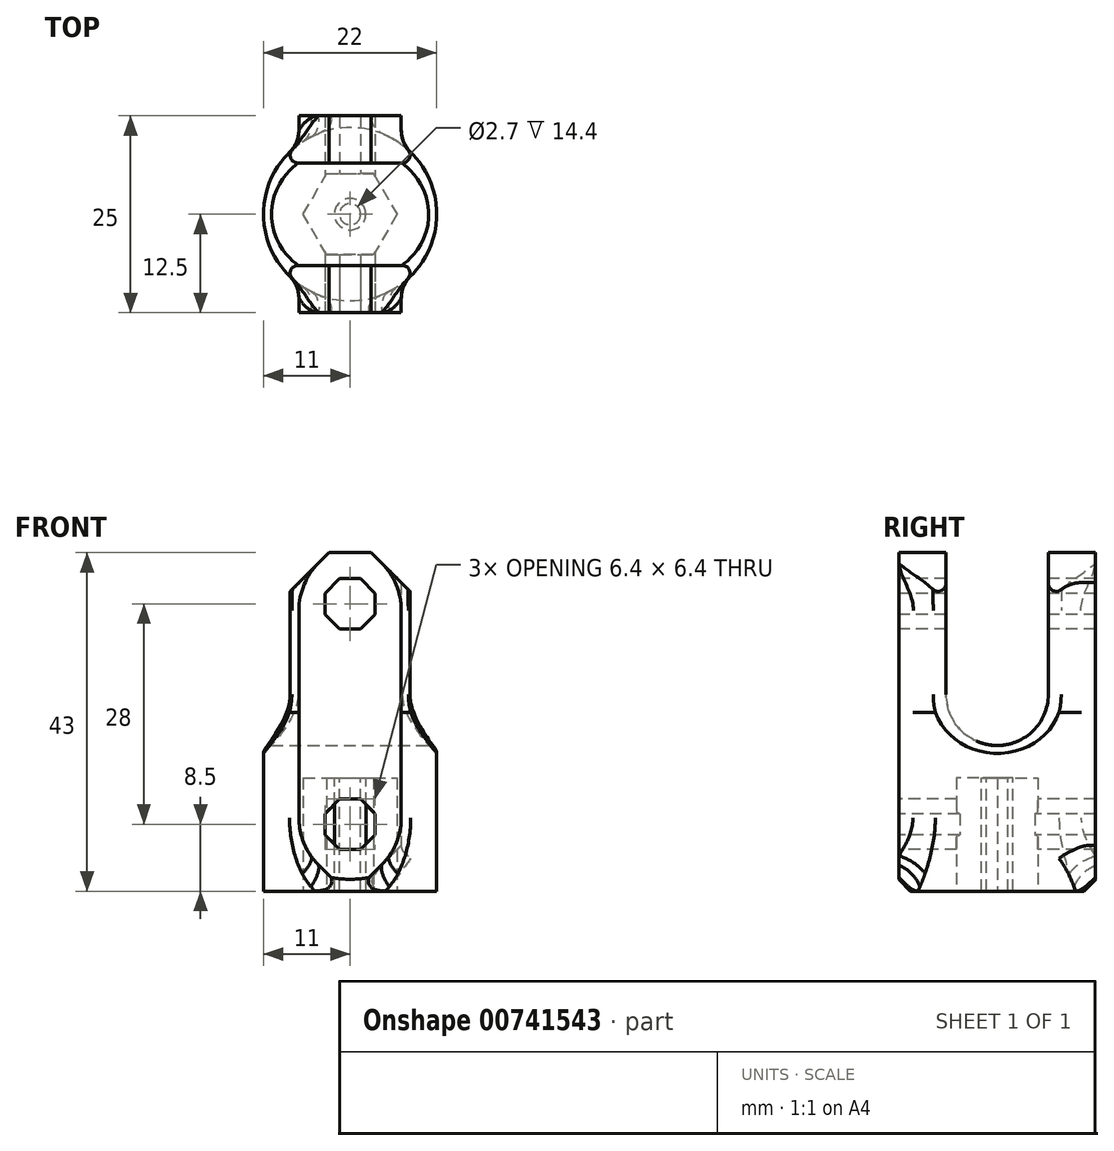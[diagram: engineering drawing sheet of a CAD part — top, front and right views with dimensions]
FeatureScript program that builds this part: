
annotation { "Feature Type Name" : "Feature", "Feature Type Description" : "" }
export const myFeature = defineFeature(function(context is Context, id is Id, definition is map)
    precondition{}
    {
        {
            var Q0;
            Q0=qCreatedBy(makeId("Top.planeOp"),FACE);
            var sketch = newSketch(context, id + "F0", { "sketchPlane" : qUnion([Q0])});
            skCircle(sketch, "E0", {"center": v(0, 0) * mm, "radius": 11 * mm});
            skCircle(sketch, "E1.cCircle", {"center": v(0, 0) * mm, "radius": 5.15 * mm, "construction": true});
            skLineSegment(sketch, "E1.0", {"start": v(-2.97, 5.15) * mm, "end": v(2.97, 5.15) * mm});
            skLineSegment(sketch, "E1.1", {"start": v(2.97, 5.15) * mm, "end": v(5.95, 0) * mm});
            skLineSegment(sketch, "E1.2", {"start": v(5.95, 0) * mm, "end": v(2.97, -5.15) * mm});
            skLineSegment(sketch, "E1.3", {"start": v(2.97, -5.15) * mm, "end": v(-2.97, -5.15) * mm});
            skLineSegment(sketch, "E1.4", {"start": v(-2.97, -5.15) * mm, "end": v(-5.95, 0) * mm});
            skLineSegment(sketch, "E1.5", {"start": v(-5.95, 0) * mm, "end": v(-2.97, 5.15) * mm});
            skPoint(sketch, "E1.0.midPoint", {"position": v(0, 5.15) * mm});
            skSolve(sketch);
        }
        {
            var Q0;
            Q0 = qSketchRegion(id + "F0", true);
            extrude(context, id + "F1", {"entities" : qUnion([Q0]), "depth" : 14 * mm, "offsetDistance" : 25 * mm});
        }
        {
            var Q0;
            Q0=makeQuery(id+"F1.opExtrude","CAP_FACE",FACE,{"disambiguationData":[OSD([sQuery(id+"F0.wireOp",EDGE,"E0"),sQuery(id+"F0.wireOp",EDGE,"E1.0"),sQuery(id+"F0.wireOp",EDGE,"E1.1"),sQuery(id+"F0.wireOp",EDGE,"E1.2"),sQuery(id+"F0.wireOp",EDGE,"E1.3"),sQuery(id+"F0.wireOp",EDGE,"E1.4"),sQuery(id+"F0.wireOp",EDGE,"E1.5")])],"isStart":false});
            var sketch = newSketch(context, id + "F2", { "sketchPlane" : qUnion([Q0])});
            skCircle(sketch, "E2.0", {"center": v(0, 0) * mm, "radius": 11 * mm});
            skSolve(sketch);
        }
        {
            var Q0;
            Q0 = qSketchRegion(id + "F2", true);
            extrude(context, id + "F3", {"entities" : qUnion([Q0]), "operationType" : NewBodyOperationType.ADD, "depth" : 29 * mm, "offsetDistance" : 25 * mm});
        }
        {
            var Q0;
            Q0=qCreatedBy(makeId("Front.planeOp"),FACE);
            var sketch = newSketch(context, id + "F4", { "sketchPlane" : qUnion([Q0])});
            skCircle(sketch, "E3.cCircle", {"center": v(0, 8.5) * mm, "radius": 6.5 * mm, "construction": true});
            skLineSegment(sketch, "E3.0", {"start": v(-2.7, 15) * mm, "end": v(2.7, 15) * mm, "construction": true});
            skLineSegment(sketch, "E3.1", {"start": v(2.7, 15) * mm, "end": v(6.5, 11.2) * mm, "construction": true});
            skLineSegment(sketch, "E3.2", {"start": v(6.5, 11.2) * mm, "end": v(6.5, 5.8) * mm});
            skLineSegment(sketch, "E3.3", {"start": v(6.5, 5.8) * mm, "end": v(2.7, 2) * mm});
            skLineSegment(sketch, "E3.4", {"start": v(2.7, 2) * mm, "end": v(-2.7, 2) * mm});
            skLineSegment(sketch, "E3.5", {"start": v(-2.7, 2) * mm, "end": v(-6.5, 5.8) * mm});
            skLineSegment(sketch, "E3.6", {"start": v(-6.5, 5.8) * mm, "end": v(-6.5, 11.2) * mm});
            skLineSegment(sketch, "E3.7", {"start": v(-6.5, 11.2) * mm, "end": v(-2.7, 15) * mm, "construction": true});
            skPoint(sketch, "E3.0.midPoint", {"position": v(0, 15) * mm});
            skPoint(sketch, "E4.0.1.0", {"position": v(0, 43) * mm});
            skLineSegment(sketch, "E4.0.1.1", {"start": v(6.5, 39.2) * mm, "end": v(6.5, 33.8) * mm});
            skLineSegment(sketch, "E4.0.1.2", {"start": v(-6.5, 33.8) * mm, "end": v(-6.5, 39.2) * mm});
            skLineSegment(sketch, "E4.0.1.3", {"start": v(-6.5, 39.2) * mm, "end": v(-2.7, 43) * mm});
            skLineSegment(sketch, "E4.0.1.4", {"start": v(2.7, 30) * mm, "end": v(-2.7, 30) * mm, "construction": true});
            skLineSegment(sketch, "E4.0.1.5", {"start": v(6.5, 33.8) * mm, "end": v(2.7, 30) * mm, "construction": true});
            skLineSegment(sketch, "E4.0.1.6", {"start": v(-2.7, 43) * mm, "end": v(2.7, 43) * mm});
            skLineSegment(sketch, "E4.0.1.7", {"start": v(2.7, 43) * mm, "end": v(6.5, 39.2) * mm});
            skLineSegment(sketch, "E4.0.1.8", {"start": v(-2.7, 30) * mm, "end": v(-6.5, 33.8) * mm, "construction": true});
            skLineSegment(sketch, "E4.direction1", {"start": v(-2.7, 2) * mm, "end": v(23.3, 2) * mm, "construction": true});
            skLineSegment(sketch, "E4.direction2", {"start": v(-2.7, 2) * mm, "end": v(-2.7, 30) * mm, "construction": true});
            skLineSegment(sketch, "E5", {"start": v(-6.5, 33.8) * mm, "end": v(-6.5, 11.2) * mm});
            skLineSegment(sketch, "E6", {"start": v(6.5, 33.8) * mm, "end": v(6.5, 11.2) * mm});
            skSolve(sketch);
        }
        {
            var Q0;
            Q0 = qSketchRegion(id + "F4", true);
            extrude(context, id + "F5", {"entities" : qUnion([Q0]), "operationType" : NewBodyOperationType.ADD, "endBound" : BoundingType.SYMMETRIC, "depth" : 25 * mm, "offsetDistance" : 25 * mm});
        }
        {
            var Q0;
            Q0=qCreatedBy(makeId("Right.planeOp"),FACE);
            var sketch = newSketch(context, id + "F6", { "sketchPlane" : qUnion([Q0])});
            skLineSegment(sketch, "E7", {"start": v(0, 43) * mm, "end": v(0, 25) * mm});
            skArc(sketch, "E8.0.startCap", {"start": v(-6.5, 43) * mm, "mid": v(0, 49.5) * mm, "end": v(6.5, 43) * mm});
            skArc(sketch, "E8.0.endCap", {"start": v(6.5, 25) * mm, "mid": v(0, 18.5) * mm, "end": v(-6.5, 25) * mm});
            skLineSegment(sketch, "E8.0.left", {"start": v(6.5, 43) * mm, "end": v(6.5, 25) * mm});
            skLineSegment(sketch, "E8.0.right", {"start": v(-6.5, 43) * mm, "end": v(-6.5, 25) * mm});
            skLineSegment(sketch, "E9", {"start": v(0, 18.5) * mm, "end": v(18, 18.5) * mm, "construction": true});
            skSolve(sketch);
        }
        {
            var Q0;
            Q0 = qSketchRegion(id + "F6", true);
            extrude(context, id + "F7", {"entities" : qUnion([Q0]), "operationType" : NewBodyOperationType.REMOVE, "endBound" : BoundingType.SYMMETRIC, "oppositeDirection" : true, "depth" : 25 * mm, "offsetDistance" : 25 * mm});
        }
        {
            var Q0;
            Q0=qCreatedBy(makeId("Front.planeOp"),FACE);
            var sketch = newSketch(context, id + "F8", { "sketchPlane" : qUnion([Q0])});
            skCircle(sketch, "E10.cCircle", {"center": v(0, 8.5) * mm, "radius": 3.2 * mm, "construction": true});
            skLineSegment(sketch, "E10.0", {"start": v(-1.33, 11.7) * mm, "end": v(1.33, 11.7) * mm});
            skLineSegment(sketch, "E10.1", {"start": v(1.33, 11.7) * mm, "end": v(3.2, 9.83) * mm});
            skLineSegment(sketch, "E10.2", {"start": v(3.2, 9.83) * mm, "end": v(3.2, 7.17) * mm});
            skLineSegment(sketch, "E10.3", {"start": v(3.2, 7.17) * mm, "end": v(1.33, 5.3) * mm});
            skLineSegment(sketch, "E10.4", {"start": v(1.33, 5.3) * mm, "end": v(-1.33, 5.3) * mm});
            skLineSegment(sketch, "E10.5", {"start": v(-1.33, 5.3) * mm, "end": v(-3.2, 7.17) * mm});
            skLineSegment(sketch, "E10.6", {"start": v(-3.2, 7.17) * mm, "end": v(-3.2, 9.83) * mm});
            skLineSegment(sketch, "E10.7", {"start": v(-3.2, 9.83) * mm, "end": v(-1.33, 11.7) * mm});
            skPoint(sketch, "E10.0.midPoint", {"position": v(0, 11.7) * mm});
            skLineSegment(sketch, "E11.0.1.0", {"start": v(-3.2, 37.83) * mm, "end": v(-1.33, 39.7) * mm});
            skLineSegment(sketch, "E11.0.1.1", {"start": v(-3.2, 35.17) * mm, "end": v(-3.2, 37.83) * mm});
            skLineSegment(sketch, "E11.0.1.2", {"start": v(-1.33, 39.7) * mm, "end": v(1.33, 39.7) * mm});
            skLineSegment(sketch, "E11.0.1.3", {"start": v(1.33, 39.7) * mm, "end": v(3.2, 37.83) * mm});
            skLineSegment(sketch, "E11.0.1.4", {"start": v(3.2, 37.83) * mm, "end": v(3.2, 35.17) * mm});
            skLineSegment(sketch, "E11.0.1.5", {"start": v(3.2, 35.17) * mm, "end": v(1.33, 33.3) * mm});
            skLineSegment(sketch, "E11.0.1.6", {"start": v(1.33, 33.3) * mm, "end": v(-1.33, 33.3) * mm});
            skLineSegment(sketch, "E11.0.1.7", {"start": v(-1.33, 33.3) * mm, "end": v(-3.2, 35.17) * mm});
            skLineSegment(sketch, "E11.direction1", {"start": v(-1.33, 5.3) * mm, "end": v(23.67, 5.3) * mm, "construction": true});
            skLineSegment(sketch, "E11.direction2", {"start": v(-1.33, 5.3) * mm, "end": v(-1.33, 33.3) * mm, "construction": true});
            skLineSegment(sketch, "E12", {"start": v(2.7, 43) * mm, "end": v(-2.7, 43) * mm});
            skLineSegment(sketch, "E13", {"start": v(-2.7, 43) * mm, "end": v(-8.87, 36.82) * mm});
            skLineSegment(sketch, "E14", {"start": v(-8.87, 36.82) * mm, "end": v(-8.87, 43.83) * mm});
            skLineSegment(sketch, "E15", {"start": v(-8.87, 43.83) * mm, "end": v(8.87, 43.83) * mm});
            skLineSegment(sketch, "E16", {"start": v(8.87, 43.83) * mm, "end": v(8.87, 36.82) * mm});
            skLineSegment(sketch, "E17", {"start": v(8.87, 36.82) * mm, "end": v(2.7, 43) * mm});
            skSolve(sketch);
        }
        {
            var Q0;
            Q0 = qSketchRegion(id + "F8", true);
            extrude(context, id + "F9", {"entities" : qUnion([Q0]), "operationType" : NewBodyOperationType.REMOVE, "endBound" : BoundingType.SYMMETRIC, "oppositeDirection" : true, "depth" : 30 * mm, "offsetDistance" : 25 * mm});
        }
        {
            var Q0;
            Q0=makeQuery(id+"F1.opExtrude","CAP_FACE",FACE,{"disambiguationData":[OSD([sQuery(id+"F0.wireOp",EDGE,"E0"),sQuery(id+"F0.wireOp",EDGE,"E1.0"),sQuery(id+"F0.wireOp",EDGE,"E1.1"),sQuery(id+"F0.wireOp",EDGE,"E1.2"),sQuery(id+"F0.wireOp",EDGE,"E1.3"),sQuery(id+"F0.wireOp",EDGE,"E1.4"),sQuery(id+"F0.wireOp",EDGE,"E1.5")])],"isStart":true});
            var sketch = newSketch(context, id + "F10", { "sketchPlane" : qUnion([Q0])});
            skCircle(sketch, "E18.cCircle", {"center": v(0, 0) * mm, "radius": 5.15 * mm, "construction": true});
            skLineSegment(sketch, "E18.0", {"start": v(2.97, 5.15) * mm, "end": v(5.95, 0) * mm});
            skLineSegment(sketch, "E18.1", {"start": v(5.95, 0) * mm, "end": v(2.97, -5.15) * mm});
            skLineSegment(sketch, "E18.2", {"start": v(2.97, -5.15) * mm, "end": v(-2.97, -5.15) * mm});
            skLineSegment(sketch, "E18.3", {"start": v(-2.97, -5.15) * mm, "end": v(-5.95, 0) * mm});
            skLineSegment(sketch, "E18.4", {"start": v(-5.95, 0) * mm, "end": v(-2.97, 5.15) * mm});
            skLineSegment(sketch, "E18.5", {"start": v(-2.97, 5.15) * mm, "end": v(2.97, 5.15) * mm});
            skPoint(sketch, "E18.0.midPoint", {"position": v(4.46, 2.57) * mm});
            skSolve(sketch);
        }
        {
            var Q0;
            Q0 = qSketchRegion(id + "F10", true);
            extrude(context, id + "F11", {"entities" : qUnion([Q0]), "operationType" : NewBodyOperationType.REMOVE, "oppositeDirection" : true, "depth" : 14.4 * mm, "offsetDistance" : 25 * mm});
        }
        {
            var Q0;
            Q0=makeQuery(id+"F7.boolean.opBoolean","INTERSECT",EDGE,{"disambiguationData":[OD(1.0)],"derivedFrom":[makeQuery(id+"F3.boolean.opBoolean","MERGE",FACE,{"derivedFrom":[makeQuery(id+"F1.opExtrude","SWEPT_FACE",FACE,{"disambiguationData":[OSD([sQuery(id+"F0.wireOp",EDGE,"E0")])]}),makeQuery(id+"F3.opExtrude","SWEPT_FACE",FACE,{"disambiguationData":[OSD([sQuery(id+"F2.wireOp",EDGE,"E2.0")])]})]}),makeQuery(id+"F7.opExtrude","SWEPT_FACE",FACE,{"disambiguationData":[OSD([sQuery(id+"F6.wireOp",EDGE,"E8.0.endCap")])]})]});
            var Q1;
            Q1=makeQuery(id+"F7.boolean.opBoolean","INTERSECT",EDGE,{"disambiguationData":[OD(1.0)],"derivedFrom":[makeQuery(id+"F3.boolean.opBoolean","MERGE",FACE,{"derivedFrom":[makeQuery(id+"F1.opExtrude","SWEPT_FACE",FACE,{"disambiguationData":[OSD([sQuery(id+"F0.wireOp",EDGE,"E0")])]}),makeQuery(id+"F3.opExtrude","SWEPT_FACE",FACE,{"disambiguationData":[OSD([sQuery(id+"F2.wireOp",EDGE,"E2.0")])]})]}),makeQuery(id+"F7.opExtrude","SWEPT_FACE",FACE,{"disambiguationData":[OSD([sQuery(id+"F6.wireOp",EDGE,"E8.0.left")])]})]});
            var Q2;
            Q2=makeQuery(id+"F7.boolean.opBoolean","INTERSECT",EDGE,{"disambiguationData":[OD(1.0)],"derivedFrom":[makeQuery(id+"F3.boolean.opBoolean","MERGE",FACE,{"derivedFrom":[makeQuery(id+"F1.opExtrude","SWEPT_FACE",FACE,{"disambiguationData":[OSD([sQuery(id+"F0.wireOp",EDGE,"E0")])]}),makeQuery(id+"F3.opExtrude","SWEPT_FACE",FACE,{"disambiguationData":[OSD([sQuery(id+"F2.wireOp",EDGE,"E2.0")])]})]}),makeQuery(id+"F7.opExtrude","SWEPT_FACE",FACE,{"disambiguationData":[OSD([sQuery(id+"F6.wireOp",EDGE,"E8.0.right")])]})]});
            var Q3;
            Q3=makeQuery(id+"F7.boolean.opBoolean","INTERSECT",EDGE,{"disambiguationData":[OD(0.0)],"derivedFrom":[makeQuery(id+"F3.boolean.opBoolean","MERGE",FACE,{"derivedFrom":[makeQuery(id+"F1.opExtrude","SWEPT_FACE",FACE,{"disambiguationData":[OSD([sQuery(id+"F0.wireOp",EDGE,"E0")])]}),makeQuery(id+"F3.opExtrude","SWEPT_FACE",FACE,{"disambiguationData":[OSD([sQuery(id+"F2.wireOp",EDGE,"E2.0")])]})]}),makeQuery(id+"F7.opExtrude","SWEPT_FACE",FACE,{"disambiguationData":[OSD([sQuery(id+"F6.wireOp",EDGE,"E8.0.endCap")])]})]});
            var Q4;
            Q4=makeQuery(id+"F7.boolean.opBoolean","INTERSECT",EDGE,{"disambiguationData":[OD(0.0)],"derivedFrom":[makeQuery(id+"F3.boolean.opBoolean","MERGE",FACE,{"derivedFrom":[makeQuery(id+"F1.opExtrude","SWEPT_FACE",FACE,{"disambiguationData":[OSD([sQuery(id+"F0.wireOp",EDGE,"E0")])]}),makeQuery(id+"F3.opExtrude","SWEPT_FACE",FACE,{"disambiguationData":[OSD([sQuery(id+"F2.wireOp",EDGE,"E2.0")])]})]}),makeQuery(id+"F7.opExtrude","SWEPT_FACE",FACE,{"disambiguationData":[OSD([sQuery(id+"F6.wireOp",EDGE,"E8.0.right")])]})]});
            var Q5;
            Q5=makeQuery(id+"F7.boolean.opBoolean","INTERSECT",EDGE,{"disambiguationData":[OD(0.0)],"derivedFrom":[makeQuery(id+"F3.boolean.opBoolean","MERGE",FACE,{"derivedFrom":[makeQuery(id+"F1.opExtrude","SWEPT_FACE",FACE,{"disambiguationData":[OSD([sQuery(id+"F0.wireOp",EDGE,"E0")])]}),makeQuery(id+"F3.opExtrude","SWEPT_FACE",FACE,{"disambiguationData":[OSD([sQuery(id+"F2.wireOp",EDGE,"E2.0")])]})]}),makeQuery(id+"F7.opExtrude","SWEPT_FACE",FACE,{"disambiguationData":[OSD([sQuery(id+"F6.wireOp",EDGE,"E8.0.left")])]})]});
            fillet(context, id + "F12", {"entities" : qUnion([Q0, Q1, Q2, Q3, Q4, Q5]), "radius" : 1 * mm, "allowEdgeOverflow" : false});
        }
        {
            var Q0;
            Q0=makeQuery(id+"F5.boolean.opBoolean","INTERSECT",EDGE,{"disambiguationData":[OD(1.0)],"derivedFrom":[makeQuery(id+"F3.boolean.opBoolean","MERGE",FACE,{"derivedFrom":[makeQuery(id+"F1.opExtrude","SWEPT_FACE",FACE,{"disambiguationData":[OSD([sQuery(id+"F0.wireOp",EDGE,"E0")])]}),makeQuery(id+"F3.opExtrude","SWEPT_FACE",FACE,{"disambiguationData":[OSD([sQuery(id+"F2.wireOp",EDGE,"E2.0")])]})]}),makeQuery(id+"F5.opExtrude","SWEPT_FACE",FACE,{"disambiguationData":[OSD([sQuery(id+"F4.wireOp",EDGE,"E3.4")])]})]});
            var Q1;
            Q1=makeQuery(id+"F5.boolean.opBoolean","INTERSECT",EDGE,{"disambiguationData":[OD(1.0)],"derivedFrom":[makeQuery(id+"F3.boolean.opBoolean","MERGE",FACE,{"derivedFrom":[makeQuery(id+"F1.opExtrude","SWEPT_FACE",FACE,{"disambiguationData":[OSD([sQuery(id+"F0.wireOp",EDGE,"E0")])]}),makeQuery(id+"F3.opExtrude","SWEPT_FACE",FACE,{"disambiguationData":[OSD([sQuery(id+"F2.wireOp",EDGE,"E2.0")])]})]}),makeQuery(id+"F5.opExtrude","SWEPT_FACE",FACE,{"disambiguationData":[OSD([sQuery(id+"F4.wireOp",EDGE,"E4.0.1.4")])]})]});
            var Q2;
            Q2=makeQuery(id+"F5.boolean.opBoolean","INTERSECT",EDGE,{"disambiguationData":[OD(0.0)],"derivedFrom":[makeQuery(id+"F3.boolean.opBoolean","MERGE",FACE,{"derivedFrom":[makeQuery(id+"F1.opExtrude","SWEPT_FACE",FACE,{"disambiguationData":[OSD([sQuery(id+"F0.wireOp",EDGE,"E0")])]}),makeQuery(id+"F3.opExtrude","SWEPT_FACE",FACE,{"disambiguationData":[OSD([sQuery(id+"F2.wireOp",EDGE,"E2.0")])]})]}),makeQuery(id+"F5.opExtrude","SWEPT_FACE",FACE,{"disambiguationData":[OSD([sQuery(id+"F4.wireOp",EDGE,"E3.4")])]})]});
            var Q3;
            Q3=makeQuery(id+"F5.boolean.opBoolean","INTERSECT",EDGE,{"disambiguationData":[OD(0.0)],"derivedFrom":[makeQuery(id+"F3.boolean.opBoolean","MERGE",FACE,{"derivedFrom":[makeQuery(id+"F1.opExtrude","SWEPT_FACE",FACE,{"disambiguationData":[OSD([sQuery(id+"F0.wireOp",EDGE,"E0")])]}),makeQuery(id+"F3.opExtrude","SWEPT_FACE",FACE,{"disambiguationData":[OSD([sQuery(id+"F2.wireOp",EDGE,"E2.0")])]})]}),makeQuery(id+"F5.opExtrude","SWEPT_FACE",FACE,{"disambiguationData":[OSD([sQuery(id+"F4.wireOp",EDGE,"E4.0.1.4")])]})]});
            var Q4;
            Q4=makeQuery(id+"F5.boolean.opBoolean","INTERSECT",EDGE,{"disambiguationData":[OD(0.0)],"derivedFrom":[makeQuery(id+"F3.boolean.opBoolean","MERGE",FACE,{"derivedFrom":[makeQuery(id+"F1.opExtrude","SWEPT_FACE",FACE,{"disambiguationData":[OSD([sQuery(id+"F0.wireOp",EDGE,"E0")])]}),makeQuery(id+"F3.opExtrude","SWEPT_FACE",FACE,{"disambiguationData":[OSD([sQuery(id+"F2.wireOp",EDGE,"E2.0")])]})]}),makeQuery(id+"F5.opExtrude","SWEPT_FACE",FACE,{"disambiguationData":[OSD([sQuery(id+"F4.wireOp",EDGE,"E3.0")])]})]});
            var Q5;
            Q5=makeQuery(id+"F5.boolean.opBoolean","INTERSECT",EDGE,{"disambiguationData":[OD(1.0)],"derivedFrom":[makeQuery(id+"F3.boolean.opBoolean","MERGE",FACE,{"derivedFrom":[makeQuery(id+"F1.opExtrude","SWEPT_FACE",FACE,{"disambiguationData":[OSD([sQuery(id+"F0.wireOp",EDGE,"E0")])]}),makeQuery(id+"F3.opExtrude","SWEPT_FACE",FACE,{"disambiguationData":[OSD([sQuery(id+"F2.wireOp",EDGE,"E2.0")])]})]}),makeQuery(id+"F5.opExtrude","SWEPT_FACE",FACE,{"disambiguationData":[OSD([sQuery(id+"F4.wireOp",EDGE,"E3.0")])]})]});
            chamfer(context, id + "F13", {"entities" : qUnion([Q0, Q1, Q2, Q3, Q4, Q5]), "width" : 2 * mm, "tangentPropagation" : true});
        }
        {
            var Q0;
            {var subQ0=sQuery(id+"F4.wireOp",EDGE,"E6");var subQ1=sQuery(id+"F4.wireOp",EDGE,"E4.0.1.1");var subQ2=sQuery(id+"F4.wireOp",EDGE,"E3.2");var subQ3=sQuery(id+"F4.wireOp",EDGE,"E4.0.1.7");Q0=makeQuery(id+"F5.boolean.opBoolean","SPLIT",EDGE,{"disambiguationData":[TD([makeQuery(id+"F5.opExtrude","CAP_FACE",FACE,{"disambiguationData":[OSD([subQ2,sQuery(id+"F4.wireOp",EDGE,"E3.3"),sQuery(id+"F4.wireOp",EDGE,"E3.4"),sQuery(id+"F4.wireOp",EDGE,"E3.5"),sQuery(id+"F4.wireOp",EDGE,"E3.6"),subQ1,sQuery(id+"F4.wireOp",EDGE,"E4.0.1.2"),sQuery(id+"F4.wireOp",EDGE,"E4.0.1.3"),sQuery(id+"F4.wireOp",EDGE,"E4.0.1.6"),subQ3,sQuery(id+"F4.wireOp",EDGE,"E5"),subQ0])],"isStart":false})])],"derivedFrom":makeQuery(id+"F5.opExtrude","SWEPT_EDGE",EDGE,{"disambiguationData":[OSD([subQ1,subQ3])]})});}
            var Q1;
            {var subQ0=sQuery(id+"F4.wireOp",EDGE,"E6");var subQ1=sQuery(id+"F4.wireOp",EDGE,"E4.0.1.1");var subQ2=sQuery(id+"F4.wireOp",EDGE,"E3.2");var subQ3=sQuery(id+"F4.wireOp",EDGE,"E3.3");Q1=makeQuery(id+"F5.boolean.opBoolean","SPLIT",EDGE,{"disambiguationData":[TD([makeQuery(id+"F5.opExtrude","CAP_FACE",FACE,{"disambiguationData":[OSD([subQ2,subQ3,sQuery(id+"F4.wireOp",EDGE,"E3.4"),sQuery(id+"F4.wireOp",EDGE,"E3.5"),sQuery(id+"F4.wireOp",EDGE,"E3.6"),subQ1,sQuery(id+"F4.wireOp",EDGE,"E4.0.1.2"),sQuery(id+"F4.wireOp",EDGE,"E4.0.1.3"),sQuery(id+"F4.wireOp",EDGE,"E4.0.1.6"),sQuery(id+"F4.wireOp",EDGE,"E4.0.1.7"),sQuery(id+"F4.wireOp",EDGE,"E5"),subQ0])],"isStart":false})])],"derivedFrom":makeQuery(id+"F5.opExtrude","SWEPT_EDGE",EDGE,{"disambiguationData":[OSD([subQ2,subQ3])]})});}
            var Q2;
            {var subQ0=sQuery(id+"F4.wireOp",EDGE,"E3.5");var subQ1=sQuery(id+"F4.wireOp",EDGE,"E5");var subQ2=sQuery(id+"F4.wireOp",EDGE,"E4.0.1.2");var subQ3=sQuery(id+"F4.wireOp",EDGE,"E3.6");Q2=makeQuery(id+"F5.boolean.opBoolean","SPLIT",EDGE,{"disambiguationData":[TD([makeQuery(id+"F5.opExtrude","CAP_FACE",FACE,{"disambiguationData":[OSD([sQuery(id+"F4.wireOp",EDGE,"E3.2"),sQuery(id+"F4.wireOp",EDGE,"E3.3"),sQuery(id+"F4.wireOp",EDGE,"E3.4"),subQ0,subQ3,sQuery(id+"F4.wireOp",EDGE,"E4.0.1.1"),subQ2,sQuery(id+"F4.wireOp",EDGE,"E4.0.1.3"),sQuery(id+"F4.wireOp",EDGE,"E4.0.1.6"),sQuery(id+"F4.wireOp",EDGE,"E4.0.1.7"),subQ1,sQuery(id+"F4.wireOp",EDGE,"E6")])],"isStart":false})])],"derivedFrom":makeQuery(id+"F5.opExtrude","SWEPT_EDGE",EDGE,{"disambiguationData":[OSD([subQ0,subQ3])]})});}
            var Q3;
            {var subQ0=sQuery(id+"F4.wireOp",EDGE,"E3.5");var subQ1=sQuery(id+"F4.wireOp",EDGE,"E5");var subQ2=sQuery(id+"F4.wireOp",EDGE,"E4.0.1.2");var subQ3=sQuery(id+"F4.wireOp",EDGE,"E3.6");Q3=makeQuery(id+"F5.boolean.opBoolean","SPLIT",EDGE,{"disambiguationData":[TD([makeQuery(id+"F5.opExtrude","CAP_FACE",FACE,{"disambiguationData":[OSD([sQuery(id+"F4.wireOp",EDGE,"E3.2"),sQuery(id+"F4.wireOp",EDGE,"E3.3"),sQuery(id+"F4.wireOp",EDGE,"E3.4"),subQ0,subQ3,sQuery(id+"F4.wireOp",EDGE,"E4.0.1.1"),subQ2,sQuery(id+"F4.wireOp",EDGE,"E4.0.1.3"),sQuery(id+"F4.wireOp",EDGE,"E4.0.1.6"),sQuery(id+"F4.wireOp",EDGE,"E4.0.1.7"),subQ1,sQuery(id+"F4.wireOp",EDGE,"E6")])],"isStart":true})])],"derivedFrom":makeQuery(id+"F5.opExtrude","SWEPT_EDGE",EDGE,{"disambiguationData":[OSD([subQ0,subQ3])]})});}
            var Q4;
            {var subQ0=sQuery(id+"F4.wireOp",EDGE,"E5");var subQ1=sQuery(id+"F4.wireOp",EDGE,"E4.0.1.2");var subQ2=sQuery(id+"F4.wireOp",EDGE,"E3.6");var subQ3=sQuery(id+"F4.wireOp",EDGE,"E4.0.1.3");Q4=makeQuery(id+"F5.boolean.opBoolean","SPLIT",EDGE,{"disambiguationData":[TD([makeQuery(id+"F5.opExtrude","CAP_FACE",FACE,{"disambiguationData":[OSD([sQuery(id+"F4.wireOp",EDGE,"E3.2"),sQuery(id+"F4.wireOp",EDGE,"E3.3"),sQuery(id+"F4.wireOp",EDGE,"E3.4"),sQuery(id+"F4.wireOp",EDGE,"E3.5"),subQ2,sQuery(id+"F4.wireOp",EDGE,"E4.0.1.1"),subQ1,subQ3,sQuery(id+"F4.wireOp",EDGE,"E4.0.1.6"),sQuery(id+"F4.wireOp",EDGE,"E4.0.1.7"),subQ0,sQuery(id+"F4.wireOp",EDGE,"E6")])],"isStart":false})])],"derivedFrom":makeQuery(id+"F5.opExtrude","SWEPT_EDGE",EDGE,{"disambiguationData":[OSD([subQ1,subQ3])]})});}
            var Q5;
            {var subQ0=sQuery(id+"F4.wireOp",EDGE,"E5");var subQ1=sQuery(id+"F4.wireOp",EDGE,"E4.0.1.3");var subQ2=sQuery(id+"F4.wireOp",EDGE,"E4.0.1.2");var subQ3=sQuery(id+"F4.wireOp",EDGE,"E3.6");Q5=makeQuery(id+"F5.boolean.opBoolean","SPLIT",EDGE,{"disambiguationData":[TD([makeQuery(id+"F5.opExtrude","CAP_FACE",FACE,{"disambiguationData":[OSD([sQuery(id+"F4.wireOp",EDGE,"E3.2"),sQuery(id+"F4.wireOp",EDGE,"E3.3"),sQuery(id+"F4.wireOp",EDGE,"E3.4"),sQuery(id+"F4.wireOp",EDGE,"E3.5"),subQ3,sQuery(id+"F4.wireOp",EDGE,"E4.0.1.1"),subQ2,subQ1,sQuery(id+"F4.wireOp",EDGE,"E4.0.1.6"),sQuery(id+"F4.wireOp",EDGE,"E4.0.1.7"),subQ0,sQuery(id+"F4.wireOp",EDGE,"E6")])],"isStart":true})])],"derivedFrom":makeQuery(id+"F5.opExtrude","SWEPT_EDGE",EDGE,{"disambiguationData":[OSD([subQ2,subQ1])]})});}
            fillet(context, id + "F14", {"entities" : qUnion([Q0, Q1, Q2, Q3, Q4, Q5]), "radius" : 8.5 * mm, "tangentPropagation" : true, "allowEdgeOverflow" : false});
        }
        {
            var Q0;
            Q0=makeQuery(id+"F5.boolean.opBoolean","INTERSECT",EDGE,{"disambiguationData":[OD(1.0)],"derivedFrom":[makeQuery(id+"F3.boolean.opBoolean","MERGE",FACE,{"derivedFrom":[makeQuery(id+"F1.opExtrude","SWEPT_FACE",FACE,{"disambiguationData":[OSD([sQuery(id+"F0.wireOp",EDGE,"E0")])]}),makeQuery(id+"F3.opExtrude","SWEPT_FACE",FACE,{"disambiguationData":[OSD([sQuery(id+"F2.wireOp",EDGE,"E2.0")])]})]}),makeQuery(id+"F5.opExtrude","SWEPT_FACE",FACE,{"disambiguationData":[OSD([sQuery(id+"F4.wireOp",EDGE,"E4.0.1.2")])]})]});
            var Q1;
            Q1=makeQuery(id+"F5.boolean.opBoolean","INTERSECT",EDGE,{"disambiguationData":[OD(1.0)],"derivedFrom":[makeQuery(id+"F3.boolean.opBoolean","MERGE",FACE,{"derivedFrom":[makeQuery(id+"F1.opExtrude","SWEPT_FACE",FACE,{"disambiguationData":[OSD([sQuery(id+"F0.wireOp",EDGE,"E0")])]}),makeQuery(id+"F3.opExtrude","SWEPT_FACE",FACE,{"disambiguationData":[OSD([sQuery(id+"F2.wireOp",EDGE,"E2.0")])]})]}),makeQuery(id+"F5.opExtrude","SWEPT_FACE",FACE,{"disambiguationData":[OSD([sQuery(id+"F4.wireOp",EDGE,"E4.0.1.8")])]})]});
            var Q2;
            Q2=makeQuery(id+"F5.boolean.opBoolean","INTERSECT",EDGE,{"disambiguationData":[OD(1.0)],"derivedFrom":[makeQuery(id+"F3.boolean.opBoolean","MERGE",FACE,{"derivedFrom":[makeQuery(id+"F1.opExtrude","SWEPT_FACE",FACE,{"disambiguationData":[OSD([sQuery(id+"F0.wireOp",EDGE,"E0")])]}),makeQuery(id+"F3.opExtrude","SWEPT_FACE",FACE,{"disambiguationData":[OSD([sQuery(id+"F2.wireOp",EDGE,"E2.0")])]})]}),makeQuery(id+"F5.opExtrude","SWEPT_FACE",FACE,{"disambiguationData":[OSD([sQuery(id+"F4.wireOp",EDGE,"E4.0.1.3")])]})]});
            var Q3;
            Q3=makeQuery(id+"F5.boolean.opBoolean","INTERSECT",EDGE,{"disambiguationData":[OD(1.0)],"derivedFrom":[makeQuery(id+"F3.boolean.opBoolean","MERGE",FACE,{"derivedFrom":[makeQuery(id+"F1.opExtrude","SWEPT_FACE",FACE,{"disambiguationData":[OSD([sQuery(id+"F0.wireOp",EDGE,"E0")])]}),makeQuery(id+"F3.opExtrude","SWEPT_FACE",FACE,{"disambiguationData":[OSD([sQuery(id+"F2.wireOp",EDGE,"E2.0")])]})]}),makeQuery(id+"F5.opExtrude","SWEPT_FACE",FACE,{"disambiguationData":[OSD([sQuery(id+"F4.wireOp",EDGE,"E3.7")])]})]});
            var Q4;
            Q4=makeQuery(id+"F5.boolean.opBoolean","INTERSECT",EDGE,{"disambiguationData":[OD(1.0)],"derivedFrom":[makeQuery(id+"F3.boolean.opBoolean","MERGE",FACE,{"derivedFrom":[makeQuery(id+"F1.opExtrude","SWEPT_FACE",FACE,{"disambiguationData":[OSD([sQuery(id+"F0.wireOp",EDGE,"E0")])]}),makeQuery(id+"F3.opExtrude","SWEPT_FACE",FACE,{"disambiguationData":[OSD([sQuery(id+"F2.wireOp",EDGE,"E2.0")])]})]}),makeQuery(id+"F5.opExtrude","SWEPT_FACE",FACE,{"disambiguationData":[OSD([sQuery(id+"F4.wireOp",EDGE,"E3.6")])]})]});
            var Q5;
            Q5=makeQuery(id+"F5.boolean.opBoolean","INTERSECT",EDGE,{"disambiguationData":[OD(1.0)],"derivedFrom":[makeQuery(id+"F3.boolean.opBoolean","MERGE",FACE,{"derivedFrom":[makeQuery(id+"F1.opExtrude","SWEPT_FACE",FACE,{"disambiguationData":[OSD([sQuery(id+"F0.wireOp",EDGE,"E0")])]}),makeQuery(id+"F3.opExtrude","SWEPT_FACE",FACE,{"disambiguationData":[OSD([sQuery(id+"F2.wireOp",EDGE,"E2.0")])]})]}),makeQuery(id+"F5.opExtrude","SWEPT_FACE",FACE,{"disambiguationData":[OSD([sQuery(id+"F4.wireOp",EDGE,"E3.5")])]})]});
            var Q6;
            Q6=makeQuery(id+"F5.boolean.opBoolean","INTERSECT",EDGE,{"disambiguationData":[OD(0.0)],"derivedFrom":[makeQuery(id+"F3.boolean.opBoolean","MERGE",FACE,{"derivedFrom":[makeQuery(id+"F1.opExtrude","SWEPT_FACE",FACE,{"disambiguationData":[OSD([sQuery(id+"F0.wireOp",EDGE,"E0")])]}),makeQuery(id+"F3.opExtrude","SWEPT_FACE",FACE,{"disambiguationData":[OSD([sQuery(id+"F2.wireOp",EDGE,"E2.0")])]})]}),makeQuery(id+"F5.opExtrude","SWEPT_FACE",FACE,{"disambiguationData":[OSD([sQuery(id+"F4.wireOp",EDGE,"E4.0.1.3")])]})]});
            var Q7;
            Q7=makeQuery(id+"F5.boolean.opBoolean","INTERSECT",EDGE,{"disambiguationData":[OD(0.0)],"derivedFrom":[makeQuery(id+"F3.boolean.opBoolean","MERGE",FACE,{"derivedFrom":[makeQuery(id+"F1.opExtrude","SWEPT_FACE",FACE,{"disambiguationData":[OSD([sQuery(id+"F0.wireOp",EDGE,"E0")])]}),makeQuery(id+"F3.opExtrude","SWEPT_FACE",FACE,{"disambiguationData":[OSD([sQuery(id+"F2.wireOp",EDGE,"E2.0")])]})]}),makeQuery(id+"F5.opExtrude","SWEPT_FACE",FACE,{"disambiguationData":[OSD([sQuery(id+"F4.wireOp",EDGE,"E4.0.1.2")])]})]});
            var Q8;
            Q8=makeQuery(id+"F5.boolean.opBoolean","INTERSECT",EDGE,{"disambiguationData":[OD(0.0)],"derivedFrom":[makeQuery(id+"F3.boolean.opBoolean","MERGE",FACE,{"derivedFrom":[makeQuery(id+"F1.opExtrude","SWEPT_FACE",FACE,{"disambiguationData":[OSD([sQuery(id+"F0.wireOp",EDGE,"E0")])]}),makeQuery(id+"F3.opExtrude","SWEPT_FACE",FACE,{"disambiguationData":[OSD([sQuery(id+"F2.wireOp",EDGE,"E2.0")])]})]}),makeQuery(id+"F5.opExtrude","SWEPT_FACE",FACE,{"disambiguationData":[OSD([sQuery(id+"F4.wireOp",EDGE,"E4.0.1.8")])]})]});
            var Q9;
            Q9=makeQuery(id+"F5.boolean.opBoolean","INTERSECT",EDGE,{"disambiguationData":[OD(0.0)],"derivedFrom":[makeQuery(id+"F3.boolean.opBoolean","MERGE",FACE,{"derivedFrom":[makeQuery(id+"F1.opExtrude","SWEPT_FACE",FACE,{"disambiguationData":[OSD([sQuery(id+"F0.wireOp",EDGE,"E0")])]}),makeQuery(id+"F3.opExtrude","SWEPT_FACE",FACE,{"disambiguationData":[OSD([sQuery(id+"F2.wireOp",EDGE,"E2.0")])]})]}),makeQuery(id+"F5.opExtrude","SWEPT_FACE",FACE,{"disambiguationData":[OSD([sQuery(id+"F4.wireOp",EDGE,"E3.7")])]})]});
            var Q10;
            Q10=makeQuery(id+"F5.boolean.opBoolean","INTERSECT",EDGE,{"disambiguationData":[OD(0.0)],"derivedFrom":[makeQuery(id+"F3.boolean.opBoolean","MERGE",FACE,{"derivedFrom":[makeQuery(id+"F1.opExtrude","SWEPT_FACE",FACE,{"disambiguationData":[OSD([sQuery(id+"F0.wireOp",EDGE,"E0")])]}),makeQuery(id+"F3.opExtrude","SWEPT_FACE",FACE,{"disambiguationData":[OSD([sQuery(id+"F2.wireOp",EDGE,"E2.0")])]})]}),makeQuery(id+"F5.opExtrude","SWEPT_FACE",FACE,{"disambiguationData":[OSD([sQuery(id+"F4.wireOp",EDGE,"E3.6")])]})]});
            var Q11;
            Q11=makeQuery(id+"F5.boolean.opBoolean","INTERSECT",EDGE,{"disambiguationData":[OD(0.0)],"derivedFrom":[makeQuery(id+"F3.boolean.opBoolean","MERGE",FACE,{"derivedFrom":[makeQuery(id+"F1.opExtrude","SWEPT_FACE",FACE,{"disambiguationData":[OSD([sQuery(id+"F0.wireOp",EDGE,"E0")])]}),makeQuery(id+"F3.opExtrude","SWEPT_FACE",FACE,{"disambiguationData":[OSD([sQuery(id+"F2.wireOp",EDGE,"E2.0")])]})]}),makeQuery(id+"F5.opExtrude","SWEPT_FACE",FACE,{"disambiguationData":[OSD([sQuery(id+"F4.wireOp",EDGE,"E3.5")])]})]});
            var Q12;
            Q12=makeQuery(id+"F5.boolean.opBoolean","INTERSECT",EDGE,{"disambiguationData":[OD(0.0)],"derivedFrom":[makeQuery(id+"F3.boolean.opBoolean","MERGE",FACE,{"derivedFrom":[makeQuery(id+"F1.opExtrude","SWEPT_FACE",FACE,{"disambiguationData":[OSD([sQuery(id+"F0.wireOp",EDGE,"E0")])]}),makeQuery(id+"F3.opExtrude","SWEPT_FACE",FACE,{"disambiguationData":[OSD([sQuery(id+"F2.wireOp",EDGE,"E2.0")])]})]}),makeQuery(id+"F5.opExtrude","SWEPT_FACE",FACE,{"disambiguationData":[OSD([sQuery(id+"F4.wireOp",EDGE,"E4.0.1.7")])]})]});
            var Q13;
            Q13=makeQuery(id+"F5.boolean.opBoolean","INTERSECT",EDGE,{"disambiguationData":[OD(0.0)],"derivedFrom":[makeQuery(id+"F3.boolean.opBoolean","MERGE",FACE,{"derivedFrom":[makeQuery(id+"F1.opExtrude","SWEPT_FACE",FACE,{"disambiguationData":[OSD([sQuery(id+"F0.wireOp",EDGE,"E0")])]}),makeQuery(id+"F3.opExtrude","SWEPT_FACE",FACE,{"disambiguationData":[OSD([sQuery(id+"F2.wireOp",EDGE,"E2.0")])]})]}),makeQuery(id+"F5.opExtrude","SWEPT_FACE",FACE,{"disambiguationData":[OSD([sQuery(id+"F4.wireOp",EDGE,"E4.0.1.1")])]})]});
            var Q14;
            Q14=makeQuery(id+"F5.boolean.opBoolean","INTERSECT",EDGE,{"disambiguationData":[OD(0.0)],"derivedFrom":[makeQuery(id+"F3.boolean.opBoolean","MERGE",FACE,{"derivedFrom":[makeQuery(id+"F1.opExtrude","SWEPT_FACE",FACE,{"disambiguationData":[OSD([sQuery(id+"F0.wireOp",EDGE,"E0")])]}),makeQuery(id+"F3.opExtrude","SWEPT_FACE",FACE,{"disambiguationData":[OSD([sQuery(id+"F2.wireOp",EDGE,"E2.0")])]})]}),makeQuery(id+"F5.opExtrude","SWEPT_FACE",FACE,{"disambiguationData":[OSD([sQuery(id+"F4.wireOp",EDGE,"E4.0.1.5")])]})]});
            var Q15;
            Q15=makeQuery(id+"F5.boolean.opBoolean","INTERSECT",EDGE,{"disambiguationData":[OD(1.0)],"derivedFrom":[makeQuery(id+"F3.boolean.opBoolean","MERGE",FACE,{"derivedFrom":[makeQuery(id+"F1.opExtrude","SWEPT_FACE",FACE,{"disambiguationData":[OSD([sQuery(id+"F0.wireOp",EDGE,"E0")])]}),makeQuery(id+"F3.opExtrude","SWEPT_FACE",FACE,{"disambiguationData":[OSD([sQuery(id+"F2.wireOp",EDGE,"E2.0")])]})]}),makeQuery(id+"F5.opExtrude","SWEPT_FACE",FACE,{"disambiguationData":[OSD([sQuery(id+"F4.wireOp",EDGE,"E4.0.1.7")])]})]});
            var Q16;
            Q16=makeQuery(id+"F5.boolean.opBoolean","INTERSECT",EDGE,{"disambiguationData":[OD(1.0)],"derivedFrom":[makeQuery(id+"F3.boolean.opBoolean","MERGE",FACE,{"derivedFrom":[makeQuery(id+"F1.opExtrude","SWEPT_FACE",FACE,{"disambiguationData":[OSD([sQuery(id+"F0.wireOp",EDGE,"E0")])]}),makeQuery(id+"F3.opExtrude","SWEPT_FACE",FACE,{"disambiguationData":[OSD([sQuery(id+"F2.wireOp",EDGE,"E2.0")])]})]}),makeQuery(id+"F5.opExtrude","SWEPT_FACE",FACE,{"disambiguationData":[OSD([sQuery(id+"F4.wireOp",EDGE,"E4.0.1.1")])]})]});
            var Q17;
            Q17=makeQuery(id+"F5.boolean.opBoolean","INTERSECT",EDGE,{"disambiguationData":[OD(1.0)],"derivedFrom":[makeQuery(id+"F3.boolean.opBoolean","MERGE",FACE,{"derivedFrom":[makeQuery(id+"F1.opExtrude","SWEPT_FACE",FACE,{"disambiguationData":[OSD([sQuery(id+"F0.wireOp",EDGE,"E0")])]}),makeQuery(id+"F3.opExtrude","SWEPT_FACE",FACE,{"disambiguationData":[OSD([sQuery(id+"F2.wireOp",EDGE,"E2.0")])]})]}),makeQuery(id+"F5.opExtrude","SWEPT_FACE",FACE,{"disambiguationData":[OSD([sQuery(id+"F4.wireOp",EDGE,"E4.0.1.5")])]})]});
            var Q18;
            Q18=makeQuery(id+"F5.boolean.opBoolean","INTERSECT",EDGE,{"disambiguationData":[OD(1.0)],"derivedFrom":[makeQuery(id+"F3.boolean.opBoolean","MERGE",FACE,{"derivedFrom":[makeQuery(id+"F1.opExtrude","SWEPT_FACE",FACE,{"disambiguationData":[OSD([sQuery(id+"F0.wireOp",EDGE,"E0")])]}),makeQuery(id+"F3.opExtrude","SWEPT_FACE",FACE,{"disambiguationData":[OSD([sQuery(id+"F2.wireOp",EDGE,"E2.0")])]})]}),makeQuery(id+"F5.opExtrude","SWEPT_FACE",FACE,{"disambiguationData":[OSD([sQuery(id+"F4.wireOp",EDGE,"E3.1")])]})]});
            var Q19;
            Q19=makeQuery(id+"F5.boolean.opBoolean","INTERSECT",EDGE,{"disambiguationData":[OD(1.0)],"derivedFrom":[makeQuery(id+"F3.boolean.opBoolean","MERGE",FACE,{"derivedFrom":[makeQuery(id+"F1.opExtrude","SWEPT_FACE",FACE,{"disambiguationData":[OSD([sQuery(id+"F0.wireOp",EDGE,"E0")])]}),makeQuery(id+"F3.opExtrude","SWEPT_FACE",FACE,{"disambiguationData":[OSD([sQuery(id+"F2.wireOp",EDGE,"E2.0")])]})]}),makeQuery(id+"F5.opExtrude","SWEPT_FACE",FACE,{"disambiguationData":[OSD([sQuery(id+"F4.wireOp",EDGE,"E3.2")])]})]});
            var Q20;
            Q20=makeQuery(id+"F5.boolean.opBoolean","INTERSECT",EDGE,{"disambiguationData":[OD(1.0)],"derivedFrom":[makeQuery(id+"F3.boolean.opBoolean","MERGE",FACE,{"derivedFrom":[makeQuery(id+"F1.opExtrude","SWEPT_FACE",FACE,{"disambiguationData":[OSD([sQuery(id+"F0.wireOp",EDGE,"E0")])]}),makeQuery(id+"F3.opExtrude","SWEPT_FACE",FACE,{"disambiguationData":[OSD([sQuery(id+"F2.wireOp",EDGE,"E2.0")])]})]}),makeQuery(id+"F5.opExtrude","SWEPT_FACE",FACE,{"disambiguationData":[OSD([sQuery(id+"F4.wireOp",EDGE,"E3.3")])]})]});
            var Q21;
            Q21=makeQuery(id+"F5.boolean.opBoolean","INTERSECT",EDGE,{"disambiguationData":[OD(0.0)],"derivedFrom":[makeQuery(id+"F3.boolean.opBoolean","MERGE",FACE,{"derivedFrom":[makeQuery(id+"F1.opExtrude","SWEPT_FACE",FACE,{"disambiguationData":[OSD([sQuery(id+"F0.wireOp",EDGE,"E0")])]}),makeQuery(id+"F3.opExtrude","SWEPT_FACE",FACE,{"disambiguationData":[OSD([sQuery(id+"F2.wireOp",EDGE,"E2.0")])]})]}),makeQuery(id+"F5.opExtrude","SWEPT_FACE",FACE,{"disambiguationData":[OSD([sQuery(id+"F4.wireOp",EDGE,"E3.1")])]})]});
            var Q22;
            Q22=makeQuery(id+"F5.boolean.opBoolean","INTERSECT",EDGE,{"disambiguationData":[OD(0.0)],"derivedFrom":[makeQuery(id+"F3.boolean.opBoolean","MERGE",FACE,{"derivedFrom":[makeQuery(id+"F1.opExtrude","SWEPT_FACE",FACE,{"disambiguationData":[OSD([sQuery(id+"F0.wireOp",EDGE,"E0")])]}),makeQuery(id+"F3.opExtrude","SWEPT_FACE",FACE,{"disambiguationData":[OSD([sQuery(id+"F2.wireOp",EDGE,"E2.0")])]})]}),makeQuery(id+"F5.opExtrude","SWEPT_FACE",FACE,{"disambiguationData":[OSD([sQuery(id+"F4.wireOp",EDGE,"E3.2")])]})]});
            var Q23;
            Q23=makeQuery(id+"F5.boolean.opBoolean","INTERSECT",EDGE,{"disambiguationData":[OD(0.0)],"derivedFrom":[makeQuery(id+"F3.boolean.opBoolean","MERGE",FACE,{"derivedFrom":[makeQuery(id+"F1.opExtrude","SWEPT_FACE",FACE,{"disambiguationData":[OSD([sQuery(id+"F0.wireOp",EDGE,"E0")])]}),makeQuery(id+"F3.opExtrude","SWEPT_FACE",FACE,{"disambiguationData":[OSD([sQuery(id+"F2.wireOp",EDGE,"E2.0")])]})]}),makeQuery(id+"F5.opExtrude","SWEPT_FACE",FACE,{"disambiguationData":[OSD([sQuery(id+"F4.wireOp",EDGE,"E3.3")])]})]});
            fillet(context, id + "F15", {"entities" : qUnion([Q0, Q1, Q2, Q3, Q4, Q5, Q6, Q7, Q8, Q9, Q10, Q11, Q12, Q13, Q14, Q15, Q16, Q17, Q18, Q19, Q20, Q21, Q22, Q23]), "radius" : 4 * mm, "tangentPropagation" : true, "allowEdgeOverflow" : false});
        }
        {
            var Q0;
            Q0=makeQuery(id+"F11.boolean.opBoolean","COPY",FACE,{"derivedFrom":makeQuery(id+"F11.opExtrude","CAP_FACE",FACE,{"disambiguationData":[OSD([sQuery(id+"F10.wireOp",EDGE,"E18.0"),sQuery(id+"F10.wireOp",EDGE,"E18.1"),sQuery(id+"F10.wireOp",EDGE,"E18.2"),sQuery(id+"F10.wireOp",EDGE,"E18.3"),sQuery(id+"F10.wireOp",EDGE,"E18.4"),sQuery(id+"F10.wireOp",EDGE,"E18.5")])],"isStart":false})});
            var sketch = newSketch(context, id + "F16", { "sketchPlane" : qUnion([Q0])});
            skCircle(sketch, "E19", {"center": v(0, 0) * mm, "radius": 2 * mm});
            skCircle(sketch, "E20", {"center": v(0, 0) * mm, "radius": 1.35 * mm});
            skSolve(sketch);
        }
        {
            var Q0;
            Q0 = qSketchRegion(id + "F16", true);
            extrude(context, id + "F17", {"entities" : qUnion([Q0]), "operationType" : NewBodyOperationType.ADD, "depth" : 14.4 * mm, "offsetDistance" : 25 * mm});
        }
    });
